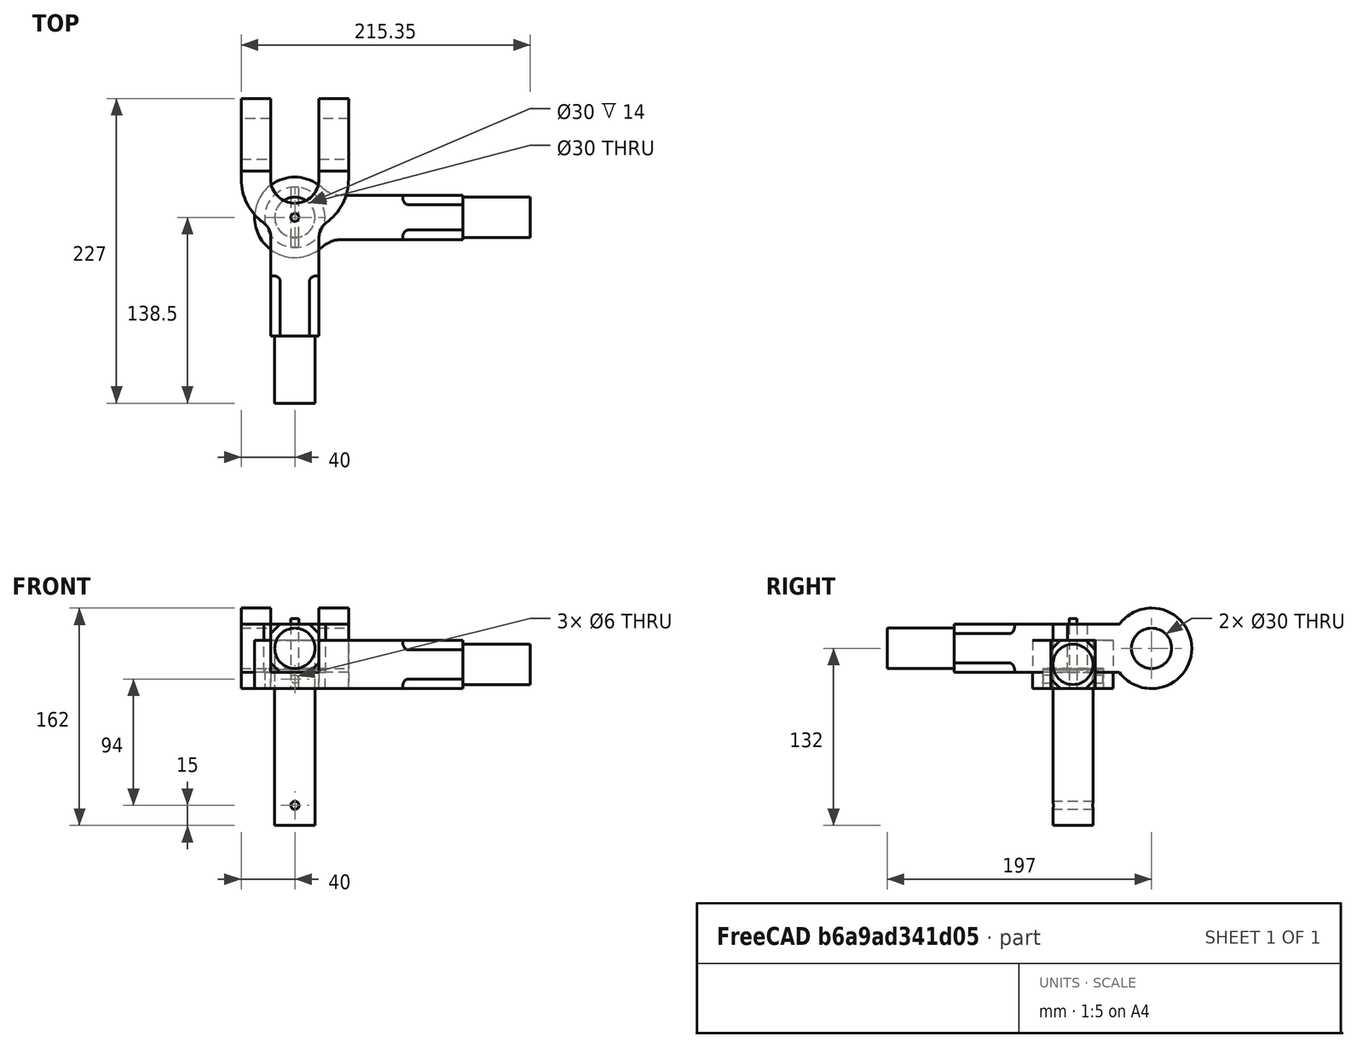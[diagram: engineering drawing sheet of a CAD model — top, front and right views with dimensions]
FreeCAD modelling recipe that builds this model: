
FCSTD DOCUMENT  (FreeCAD 1.0R39319 (Git))
Label: kunckle joint assembly and parts
License: All rights reserved
LicenseURL: https://en.wikipedia.org/wiki/All_rights_reserved
objects: TechDraw::DrawViewDimension×15, Sketcher::SketchObject×14, PartDesign::Pad×9, PartDesign::Pocket×6, PartDesign::Body×5, App::Link×5, App::FeaturePython×5, TechDraw::DrawProjGroupItem×4, PartDesign::Fillet×3, Assembly::JointGroup×1, Assembly::AssemblyObject×1, TechDraw::DrawSVGTemplate×1, TechDraw::DrawProjGroup×1, TechDraw::DrawPage×1
note: 106 computed .brp shape members not serialized (recipe doc carries the construction recipe); baked Part::Feature solids carry a one-line shape summary decoded from their .brp

FEATURE [Sketcher::SketchObject] Sketch
  ArcFitTolerance = 1e-06
  AttachmentSupport = -> [XY_Plane]
  FullyConstrained = true
  MakeInternals = false
  MapMode = 5
  sketch-geometry (7):
    g0: ArcOfCircle CenterX=0 CenterY=0 CenterZ=0 NormalX=0 NormalY=0 NormalZ=1 AngleXU=0 Radius=30 StartAngle=0.840092 EndAngle=5.44179
    g1: Circle CenterX=0 CenterY=0 CenterZ=0 NormalX=0 NormalY=0 NormalZ=1 AngleXU=0 Radius=15
    g2: LineSegment StartX=35.3005 StartY=-16.5231 StartZ=0 EndX=125.352 EndY=-16.5231 EndZ=0
    g3: LineSegment StartX=125.352 StartY=-16.5231 StartZ=0 EndX=125.352 EndY=16.4769 EndZ=0
    g4: LineSegment StartX=125.352 StartY=16.4769 StartZ=0 EndX=35.3521 EndY=16.4769 EndZ=0
    g5: ArcOfCircle CenterX=35.3521 CenterY=39.4473 CenterZ=0 NormalX=0 NormalY=0 NormalZ=1 AngleXU=0 Radius=22.9703 StartAngle=3.98168 EndAngle=4.71239
    g6: ArcOfCircle CenterX=35.3005 CenterY=-39.4934 CenterZ=0 NormalX=0 NormalY=0 NormalZ=1 AngleXU=0 Radius=22.9703 StartAngle=1.5708 EndAngle=2.30019
  constraints (18):
    c: Coincident(g0,g-1)
    c: Coincident(g1,g0)
    c: Diameter(g1) = 30
    c: Diameter(g0) = 60
    c: Coincident(g2,g3)
    c: Coincident(g3,g4)
    c: Vertical(g3)
    c: Horizontal(g2)
    c: Horizontal(g4)
    c: DistanceY(g3,g3) = 33
    c: Tangent(g0,g5) = 1.5708
    c: Tangent(g4,g5) = 1.5708
    c: Tangent(g0,g6) = 1.5708
    c: Tangent(g2,g6) = 1.5708
    c: Equal(g5,g6)
    c: Block(g5)
    c: Block(g6)
    c: DistanceX(g4,g4) = 90
FEATURE [PartDesign::Pad] Pad
  Direction = (0,0,1)
  Length = 36
  Length2 = 10
  Profile = -> Sketch
  ReferenceAxis = -> Sketch [N_Axis]
  Refine = true
  Suppressed = false
  Type = 0
FEATURE [Sketcher::SketchObject] Sketch001
  ArcFitTolerance = 1e-06
  AttachmentSupport = -> [Pad]
  ExternalGeometry = -> [Pad]
  FullyConstrained = true
  MakeInternals = false
  MapMode = 5
  Placement = pos=(125.352,0,0) rot=(0.57735,0.57735,0.57735;2.0944rad)
  sketch-geometry (1):
    g0: Circle CenterX=-0.0230899 CenterY=18 CenterZ=0 NormalX=0 NormalY=0 NormalZ=1 AngleXU=0 Radius=15
  constraints (2):
    c: Diameter(g0) = 30
    c: Symmetric(g-4,g-3,g0)
FEATURE [PartDesign::Pad] Pad001
  BaseFeature = -> Pad
  Direction = (1,0,0)
  Length = 50
  Length2 = 10
  Profile = -> Sketch001
  ReferenceAxis = -> Sketch001 [N_Axis]
  Refine = true
  Suppressed = false
  Type = 0
FEATURE [Sketcher::SketchObject] Sketch002
  ArcFitTolerance = 1e-06
  AttachmentSupport = -> [XY_Plane001]
  FullyConstrained = true
  MakeInternals = false
  MapMode = 5
  sketch-geometry (2):
    g0: Circle CenterX=0 CenterY=0 CenterZ=0 NormalX=0 NormalY=0 NormalZ=1 AngleXU=0 Radius=22.5
    g1: Circle CenterX=0 CenterY=0 CenterZ=0 NormalX=0 NormalY=0 NormalZ=1 AngleXU=0 Radius=15
  constraints (4):
    c: Coincident(g0,g-1)
    c: Coincident(g1,g0)
    c: Diameter(g0) = 45
    c: Diameter(g1) = 30
FEATURE [PartDesign::Pad] Pad002
  Direction = (0,0,1)
  Length = 14
  Length2 = 10
  Profile = -> Sketch002
  ReferenceAxis = -> Sketch002 [N_Axis]
  Refine = true
  Suppressed = false
  Type = 0
FEATURE [Sketcher::SketchObject] Sketch003
  ArcFitTolerance = 1e-06
  AttachmentSupport = -> [XZ_Plane001]
  FullyConstrained = true
  MakeInternals = false
  MapMode = 5
  Placement = pos=(0,0,0) rot=(1,0,0;1.5708rad)
  sketch-geometry (1):
    g0: Circle CenterX=0 CenterY=7 CenterZ=0 NormalX=0 NormalY=0 NormalZ=1 AngleXU=0 Radius=3
  constraints (3):
    c: PointOnObject(g0,g-2)
    c: Diameter(g0) = 6
    c: DistanceY(g-1,g0) = 7
FEATURE [PartDesign::Pocket] Pocket
  BaseFeature = -> Pad002
  Direction = (0,1,-2e-16)
  Length = 5
  Length2 = 5
  Midplane = true
  Profile = -> Sketch003
  ReferenceAxis = -> Sketch003 [N_Axis]
  Refine = true
  Suppressed = false
  Type = 1
FEATURE [PartDesign::Body] Body001  label="Collar"
  AllowCompound = false
  Group = -> [Sketch002,Pad002,Sketch003,Pocket]
  Origin = -> Origin001
  Tip = -> Pocket
FEATURE [Sketcher::SketchObject] Sketch004
  ArcFitTolerance = 1e-06
  AttachmentSupport = -> [XY_Plane002]
  FullyConstrained = true
  MakeInternals = false
  MapMode = 5
  sketch-geometry (1):
    g0: Circle CenterX=0 CenterY=0 CenterZ=0 NormalX=0 NormalY=0 NormalZ=1 AngleXU=0 Radius=22.5
  constraints (2):
    c: Coincident(g0,g-1)
    c: Diameter(g0) = 45
FEATURE [PartDesign::Pad] Pad003
  Direction = (0,0,1)
  Length = 15
  Length2 = 10
  Profile = -> Sketch004
  ReferenceAxis = -> Sketch004 [N_Axis]
  Refine = true
  Suppressed = false
  Type = 0
FEATURE [Sketcher::SketchObject] Sketch005
  ArcFitTolerance = 1e-06
  AttachmentSupport = -> [Pad003]
  FullyConstrained = true
  MakeInternals = false
  MapMode = 5
  Placement = pos=(0,0,0) rot=(1,0,0;3.14159rad)
  sketch-geometry (1):
    g0: Circle CenterX=0 CenterY=0 CenterZ=0 NormalX=0 NormalY=0 NormalZ=1 AngleXU=0 Radius=15
  constraints (2):
    c: Coincident(g0,g-1)
    c: Diameter(g0) = 30
FEATURE [PartDesign::Pad] Pad004
  BaseFeature = -> Pad003
  Direction = (0,0,-1)
  Length = 102
  Length2 = 10
  Profile = -> Sketch005
  ReferenceAxis = -> Sketch005 [N_Axis]
  Refine = true
  Suppressed = false
  Type = 0
FEATURE [Sketcher::SketchObject] Sketch006
  ArcFitTolerance = 1e-06
  AttachmentSupport = -> [XZ_Plane002]
  ExternalGeometry = -> [Pad004]
  FullyConstrained = true
  MakeInternals = false
  MapMode = 5
  Placement = pos=(0,0,0) rot=(1,0,0;1.5708rad)
  sketch-geometry (1):
    g0: Circle CenterX=0 CenterY=-87 CenterZ=0 NormalX=0 NormalY=0 NormalZ=1 AngleXU=0 Radius=3
  constraints (3):
    c: PointOnObject(g0,g-2)
    c: Diameter(g0) = 6
    c: Distance(g0,g-3) = 15
FEATURE [PartDesign::Pocket] Pocket001
  BaseFeature = -> Pad004
  Direction = (0,1,-2e-16)
  Length = 5
  Length2 = 5
  Midplane = true
  Profile = -> Sketch006
  ReferenceAxis = -> Sketch006 [N_Axis]
  Refine = true
  Suppressed = false
  Type = 1
FEATURE [PartDesign::Body] Body002  label="kunckle_pin"
  AllowCompound = false
  Group = -> [Sketch004,Pad003,Sketch005,Pad004,Sketch006,Pocket001]
  Origin = -> Origin002
  Tip = -> Pocket001
FEATURE [Sketcher::SketchObject] Sketch007
  ArcFitTolerance = 1e-06
  AttachmentSupport = -> [XY_Plane003]
  FullyConstrained = true
  MakeInternals = false
  MapMode = 5
  sketch-geometry (1):
    g0: Circle CenterX=0 CenterY=0 CenterZ=0 NormalX=0 NormalY=0 NormalZ=1 AngleXU=0 Radius=3
  constraints (2):
    c: Coincident(g0,g-1)
    c: Diameter(g0) = 6
FEATURE [PartDesign::Pad] Pad005
  Direction = (0,0,1)
  Length = 52
  Length2 = 10
  Profile = -> Sketch007
  ReferenceAxis = -> Sketch007 [N_Axis]
  Refine = true
  Suppressed = false
  Type = 0
FEATURE [PartDesign::Body] Body003  label="taper_pin"
  AllowCompound = false
  Group = -> [Sketch007,Pad005]
  Origin = -> Origin003
  Tip = -> Pad005
FEATURE [Sketcher::SketchObject] Sketch008
  ArcFitTolerance = 1e-06
  AttachmentSupport = -> [Pad001]
  ExternalGeometry = -> [Pad001]
  FullyConstrained = true
  MakeInternals = false
  MapMode = 5
  Placement = pos=(125.352,0,0) rot=(0.57735,0.57735,0.57735;2.0944rad)
  sketch-geometry (12):
    g0: LineSegment StartX=-16.5231 StartY=36 StartZ=0 EndX=-16.5231 EndY=28.9289 EndZ=0
    g1: LineSegment StartX=-16.5231 StartY=28.9289 StartZ=0 EndX=-9.45202 EndY=36 EndZ=0
    g2: LineSegment StartX=-16.5231 StartY=36 StartZ=0 EndX=-9.45202 EndY=36 EndZ=0
    g3: LineSegment StartX=-16.5231 StartY=7.07107 StartZ=0 EndX=-16.5231 EndY=0 EndZ=0
    g4: LineSegment StartX=-16.5231 StartY=0 StartZ=0 EndX=-9.45202 EndY=0 EndZ=0
    g5: LineSegment StartX=-9.45202 StartY=0 StartZ=0 EndX=-16.5231 EndY=7.07107 EndZ=0
    g6: LineSegment StartX=16.5231 StartY=28.9753 StartZ=0 EndX=9.45202 EndY=36 EndZ=0
    g7: LineSegment StartX=16.4769 StartY=36 StartZ=0 EndX=9.45202 EndY=36 EndZ=0
    g8: LineSegment StartX=16.4769 StartY=36 StartZ=0 EndX=16.5231 EndY=28.9753 EndZ=0
    g9: LineSegment StartX=9.40584 StartY=0 StartZ=0 EndX=16.4769 EndY=7.07107 EndZ=0
    g10: LineSegment StartX=16.4769 StartY=7.07107 StartZ=0 EndX=16.4769 EndY=0 EndZ=0
    g11: LineSegment StartX=16.4769 StartY=0 StartZ=0 EndX=9.40584 EndY=0 EndZ=0
  constraints (30):
    c: Coincident(g0,g-5)
    c: PointOnObject(g0,g-5)
    c: Coincident(g1,g0)
    c: Coincident(g2,g0)
    c: Coincident(g2,g1)
    c: PointOnObject(g1,g-3)
    c: PointOnObject(g3,g-5)
    c: Coincident(g3,g-5)
    c: Coincident(g3,g4)
    c: PointOnObject(g4,g-1)
    c: Coincident(g4,g5)
    c: Coincident(g5,g3)
    c: Equal(g2,g0)
    c: Distance(g1,g1) = 10
    c: Distance(g5,g5) = 10
    c: Equal(g3,g4)
    c: Coincident(g6,g8)
    c: Coincident(g7,g8)
    c: Coincident(g7,g6)
    c: Equal(g7,g8)
    c: Coincident(g10,g11)
    c: Coincident(g11,g9)
    c: Coincident(g9,g10)
    c: Equal(g10,g11)
    c: Block(g6)
    c: Coincident(g10,g-4)
    c: PointOnObject(g9,g-1)
    c: Coincident(g7,g-4)
    c: PointOnObject(g9,g-4)
    c: Distance(g9,g9) = 10
FEATURE [PartDesign::Pocket] Pocket002
  BaseFeature = -> Pad001
  Direction = (-1,0,0)
  Length = 45
  Length2 = 5
  Profile = -> Sketch008
  ReferenceAxis = -> Sketch008 [N_Axis]
  Refine = true
  Suppressed = false
  Type = 0
FEATURE [PartDesign::Fillet] Fillet
  Base = -> Pocket002 [Edge46,Edge44]
  BaseFeature = -> Pocket002
  Radius = 4
  Refine = true
  SupportTransform = false
  Suppressed = false
  UseAllEdges = false
FEATURE [PartDesign::Fillet] Fillet001
  Base = -> Fillet [Edge36,Edge52]
  BaseFeature = -> Fillet
  Radius = 4
  Refine = true
  SupportTransform = false
  Suppressed = false
  UseAllEdges = false
FEATURE [PartDesign::Body] Body  label="Single_eye"
  AllowCompound = false
  Group = -> [Sketch,Pad,Sketch001,Pad001,Sketch008,Pocket002,Fillet,Fillet001]
  Origin = -> Origin
  Tip = -> Fillet001
FEATURE [Sketcher::SketchObject] Sketch009
  ArcFitTolerance = 1e-06
  AttachmentSupport = -> [XY_Plane004]
  FullyConstrained = true
  MakeInternals = false
  MapMode = 5
  sketch-geometry (5):
    g0: LineSegment StartX=-40 StartY=88.5 StartZ=0 EndX=-40 EndY=-88.5 EndZ=0
    g1: LineSegment StartX=-40 StartY=-88.5 StartZ=0 EndX=40 EndY=-88.5 EndZ=0
    g2: LineSegment StartX=40 StartY=-88.5 StartZ=0 EndX=40 EndY=88.5 EndZ=0
    g3: LineSegment StartX=40 StartY=88.5 StartZ=0 EndX=-40 EndY=88.5 EndZ=0
    g4: GeomPoint [constr] X=0 Y=0 Z=0
  constraints (12):
    c: Coincident(g0,g1)
    c: Coincident(g1,g2)
    c: Coincident(g2,g3)
    c: Coincident(g3,g0)
    c: Vertical(g0)
    c: Vertical(g2)
    c: Horizontal(g1)
    c: Horizontal(g3)
    c: Symmetric(g2,g0,g4)
    c: Coincident(g4,g-1)
    c: DistanceY(g2,g2) = 177
    c: DistanceX(g3,g3) = 80
FEATURE [PartDesign::Pad] Pad006
  Direction = (0,0,1)
  Length = 60
  Length2 = 10
  Profile = -> Sketch009
  ReferenceAxis = -> Sketch009 [N_Axis]
  Refine = true
  Suppressed = false
  Type = 0
FEATURE [PartDesign::Pad] Pad007
  BaseFeature = -> Pad006
  Direction = (0,0,1)
  Length = 5
  Length2 = 10
  Profile = -> Sketch009
  ReferenceAxis = -> Sketch009 [N_Axis]
  Refine = true
  Suppressed = false
  Type = 0
FEATURE [Sketcher::SketchObject] Sketch010
  ArcFitTolerance = 1e-06
  AttachmentSupport = -> [Pad006]
  ExternalGeometry = -> [Pad006]
  FullyConstrained = false
  MakeInternals = false
  MapMode = 5
  Placement = pos=(0,0,0) rot=(1,0,0;3.14159rad)
  sketch-geometry (14):
    g0: ArcOfCircle CenterX=0 CenterY=-28.5 CenterZ=0 NormalX=0 NormalY=0 NormalZ=1 AngleXU=0 Radius=40 StartAngle=-9e-16 EndAngle=0.954279
    g1: ArcOfCircle CenterX=0 CenterY=-28.5 CenterZ=0 NormalX=0 NormalY=0 NormalZ=1 AngleXU=0 Radius=18 StartAngle=2e-16 EndAngle=3.14159
    g2: LineSegment StartX=-18 StartY=88.5 StartZ=0 EndX=-18 EndY=15.1917 EndZ=0
    g3: LineSegment StartX=18 StartY=88.5 StartZ=0 EndX=18 EndY=14.9616 EndZ=0
    g4: LineSegment StartX=-18 StartY=-28.5 StartZ=0 EndX=-18 EndY=-88.5 EndZ=0
    g5: LineSegment StartX=18 StartY=-28.5 StartZ=0 EndX=18 EndY=-88.5 EndZ=0
    g6: LineSegment StartX=-18 StartY=-88.5 StartZ=0 EndX=18 EndY=-88.5 EndZ=0
    g7: LineSegment StartX=-18 StartY=88.5 StartZ=0 EndX=-40 EndY=88.5 EndZ=0
    g8: LineSegment StartX=-40 StartY=88.5 StartZ=0 EndX=-40 EndY=-28.5 EndZ=0
    g9: LineSegment StartX=18 StartY=88.5 StartZ=0 EndX=40 EndY=88.5 EndZ=0
    g10: LineSegment StartX=40 StartY=88.5 StartZ=0 EndX=40 EndY=-28.5 EndZ=0
    g11: ArcOfCircle CenterX=0 CenterY=-28.5 CenterZ=0 NormalX=0 NormalY=0 NormalZ=1 AngleXU=0 Radius=40 StartAngle=2.19011 EndAngle=3.14159
    g12: ArcOfCircle CenterX=31.2806 CenterY=14.625 CenterZ=0 NormalX=0 NormalY=0 NormalZ=1 AngleXU=0 Radius=13.2849 StartAngle=3.11625 EndAngle=4.05167
    g13: ArcOfCircle CenterX=-31.2733 CenterY=14.636 CenterZ=0 NormalX=0 NormalY=0 NormalZ=1 AngleXU=0 Radius=13.2849 StartAngle=5.36376 EndAngle=6.32502
  constraints (33):
    c: Coincident(g1,g0)
    c: Diameter(g1) = 36
    c: PointOnObject(g2,g-5)
    c: Vertical(g2)
    c: PointOnObject(g3,g-5)
    c: Vertical(g3)
    c: PointOnObject(g4,g-6)
    c: Vertical(g4)
    c: PointOnObject(g5,g-6)
    c: Vertical(g5)
    c: Distance(g3,g2) = 36
    c: Distance(g-2,g2) = 18
    c: Tangent(g1,g4) = -1.5708
    c: Tangent(g1,g5) = 1.5708
    c: Coincident(g6,g4)
    c: Coincident(g6,g5)
    c: Coincident(g2,g7)
    c: Coincident(g7,g-5)
    c: Coincident(g7,g8)
    c: Coincident(g3,g9)
    c: Coincident(g9,g-5)
    c: Coincident(g9,g10)
    c: Vertical(g10)
    c: Block(g7)
    c: Block(g8)
    c: Block(g10)
    c: Block(g11)
    c: Block(g0)
    c: Equal(g13,g12)
    c: Coincident(g3,g12)
    c: Coincident(g12,g0)
    c: Coincident(g13,g2)
    c: Coincident(g11,g13)
FEATURE [PartDesign::Pocket] Pocket003
  BaseFeature = -> Pad007
  Direction = (0,0,1)
  Length = 5
  Length2 = 5
  Profile = -> Sketch010
  ReferenceAxis = -> Sketch010 [N_Axis]
  Refine = true
  Suppressed = false
  Type = 1
FEATURE [Sketcher::SketchObject] Sketch011
  ArcFitTolerance = 1e-06
  AttachmentSupport = -> [Pocket003]
  ExternalGeometry = -> [Pocket003]
  FullyConstrained = false
  MakeInternals = false
  MapMode = 5
  Placement = pos=(40,0,0) rot=(0.57735,0.57735,0.57735;2.0944rad)
  sketch-geometry (11):
    g0: ArcOfCircle CenterX=58.5 CenterY=30 CenterZ=0 NormalX=0 NormalY=0 NormalZ=1 AngleXU=0 Radius=30 StartAngle=3.78509 EndAngle=8.78128
    g1: Circle CenterX=58.5 CenterY=30 CenterZ=0 NormalX=0 NormalY=0 NormalZ=1 AngleXU=0 Radius=15
    g2: LineSegment StartX=34.5 StartY=48 StartZ=0 EndX=-88.5 EndY=48 EndZ=0
    g3: LineSegment StartX=-88.5 StartY=12 StartZ=0 EndX=34.5 EndY=12 EndZ=0
    g4: LineSegment StartX=-88.5 StartY=12 StartZ=0 EndX=-88.5 EndY=0 EndZ=0
    g5: LineSegment StartX=-88.5 StartY=0 StartZ=0 EndX=58.5 EndY=0 EndZ=0
    g6: LineSegment StartX=-88.5 StartY=48 StartZ=0 EndX=-88.5 EndY=60 EndZ=0
    g7: LineSegment StartX=-88.5 StartY=60 StartZ=0 EndX=58.5 EndY=60 EndZ=0
    g8: LineSegment StartX=58.5 StartY=60 StartZ=0 EndX=88.5 EndY=60 EndZ=0
    g9: LineSegment StartX=88.5 StartY=60 StartZ=0 EndX=88.5 EndY=0 EndZ=0
    g10: LineSegment StartX=88.5 StartY=0 StartZ=0 EndX=58.5 EndY=0 EndZ=0
  constraints (25):
    c: Coincident(g1,g0)
    c: Diameter(g0) = 60
    c: Diameter(g1) = 30
    c: Tangent(g0,g-4)
    c: Tangent(g-3,g0)
    c: Horizontal(g2)
    c: Horizontal(g3)
    c: Distance(g3,g2) = 36
    c: PointOnObject(g2,g-5)
    c: Coincident(g0,g2)
    c: Coincident(g0,g3)
    c: Coincident(g4,g-5)
    c: Coincident(g4,g5)
    c: PointOnObject(g5,g0)
    c: Horizontal(g5)
    c: Coincident(g6,g2)
    c: Coincident(g6,g-5)
    c: Coincident(g7,g6)
    c: Symmetric(g-3,g-3,g7)
    c: Coincident(g8,g-4)
    c: Horizontal(g8)
    c: Coincident(g8,g9)
    c: Coincident(g9,g-4)
    c: Coincident(g9,g10)
    c: Coincident(g10,g5)
FEATURE [PartDesign::Pocket] Pocket004
  BaseFeature = -> Pocket003
  Direction = (-1,0,0)
  Length = 5
  Length2 = 5
  Profile = -> Sketch011
  ReferenceAxis = -> Sketch011 [N_Axis]
  Refine = true
  Suppressed = false
  Type = 1
FEATURE [Sketcher::SketchObject] Sketch012
  ArcFitTolerance = 1e-06
  AttachmentSupport = -> [Pocket004]
  ExternalGeometry = -> [Pocket004]
  FullyConstrained = true
  MakeInternals = false
  MapMode = 5
  Placement = pos=(0,-88.5,0) rot=(1,0,0;1.5708rad)
  sketch-geometry (1):
    g0: Circle CenterX=2.4e-15 CenterY=30 CenterZ=0 NormalX=0 NormalY=0 NormalZ=1 AngleXU=0 Radius=15
  constraints (2):
    c: Symmetric(g-3,g-4,g0)
    c: Diameter(g0) = 30
FEATURE [PartDesign::Pad] Pad008
  BaseFeature = -> Pocket004
  Direction = (0,-1,2e-16)
  Length = 50
  Length2 = 10
  Profile = -> Sketch012
  ReferenceAxis = -> Sketch012 [N_Axis]
  Refine = true
  Suppressed = false
  Type = 0
FEATURE [Sketcher::SketchObject] Sketch013
  ArcFitTolerance = 1e-06
  AttachmentSupport = -> [Pad008]
  ExternalGeometry = -> [Pad008]
  FullyConstrained = true
  MakeInternals = false
  MapMode = 5
  Placement = pos=(0,-88.5,0) rot=(1,0,0;1.5708rad)
  sketch-geometry (12):
    g0: LineSegment StartX=-18 StartY=48 StartZ=0 EndX=-18 EndY=40.9289 EndZ=0
    g1: LineSegment StartX=-18 StartY=40.9289 StartZ=0 EndX=-10.9289 EndY=48 EndZ=0
    g2: LineSegment StartX=-10.9289 StartY=48 StartZ=0 EndX=-18 EndY=48 EndZ=0
    g3: LineSegment StartX=10.9289 StartY=48 StartZ=0 EndX=18 EndY=40.9289 EndZ=0
    g4: LineSegment StartX=18 StartY=40.9289 StartZ=0 EndX=18 EndY=48 EndZ=0
    g5: LineSegment StartX=18 StartY=48 StartZ=0 EndX=10.9289 EndY=48 EndZ=0
    g6: LineSegment StartX=-18 StartY=19.0711 StartZ=0 EndX=-18 EndY=12 EndZ=0
    g7: LineSegment StartX=-18 StartY=12 StartZ=0 EndX=-10.9289 EndY=12 EndZ=0
    g8: LineSegment StartX=-10.9289 StartY=12 StartZ=0 EndX=-18 EndY=19.0711 EndZ=0
    g9: LineSegment StartX=18 StartY=19.0711 StartZ=0 EndX=18 EndY=12 EndZ=0
    g10: LineSegment StartX=18 StartY=12 StartZ=0 EndX=10.9289 EndY=12 EndZ=0
    g11: LineSegment StartX=10.9289 StartY=12 StartZ=0 EndX=18 EndY=19.0711 EndZ=0
  constraints (32):
    c: Coincident(g-3,g0)
    c: Vertical(g0)
    c: Coincident(g0,g1)
    c: PointOnObject(g1,g-3)
    c: Coincident(g1,g2)
    c: Coincident(g2,g0)
    c: PointOnObject(g3,g-3)
    c: PointOnObject(g3,g-4)
    c: Coincident(g3,g4)
    c: Coincident(g4,g-4)
    c: Coincident(g4,g5)
    c: Coincident(g5,g3)
    c: PointOnObject(g6,g-6)
    c: Coincident(g6,g-6)
    c: Coincident(g6,g7)
    c: PointOnObject(g7,g-5)
    c: Coincident(g7,g8)
    c: Coincident(g8,g6)
    c: PointOnObject(g9,g-4)
    c: Coincident(g9,g-5)
    c: Coincident(g9,g10)
    c: PointOnObject(g10,g-5)
    c: Coincident(g10,g11)
    c: Coincident(g11,g9)
    c: Distance(g1,g1) = 10
    c: Equal(g0,g2)
    c: Equal(g6,g7)
    c: Equal(g10,g9)
    c: Distance(g3,g3) = 10
    c: Distance(g11,g11) = 10
    c: Distance(g8,g8) = 10
    c: Equal(g4,g5)
FEATURE [PartDesign::Pocket] Pocket005
  BaseFeature = -> Pad008
  Direction = (0,1,-2e-16)
  Length = 45
  Length2 = 5
  Profile = -> Sketch013
  ReferenceAxis = -> Sketch013 [N_Axis]
  Refine = true
  Suppressed = false
  Type = 0
FEATURE [PartDesign::Fillet] Fillet002
  Base = -> Pocket005 [Edge83,Edge84,Edge64,Edge72]
  BaseFeature = -> Pocket005
  Radius = 4
  Refine = true
  SupportTransform = false
  Suppressed = false
  UseAllEdges = false
FEATURE [PartDesign::Body] Body004  label="double eye"
  AllowCompound = false
  Group = -> [Sketch009,Pad006,Pad007,Sketch010,Pocket003,Sketch011,Pocket004,Sketch012,Pad008,Sketch013,Pocket005,Fillet002]
  Origin = -> Origin004
  Tip = -> Fillet002
FEATURE [App::Link] kunckle_pin  label="kunckle_pin001"
  LinkedObject = -> Body002
FEATURE [App::FeaturePython] GroundedJoint  # Assembly grounded joint (typed FeaturePython)
  ObjectToGround = -> kunckle_pin
FEATURE [App::Link] double_eye  label="double eye001"
  LinkPlacement = pos=(-30.1645,58.4153,-40) rot=(0.707106,0.000995,0.707106;3.14358rad)
  LinkedObject = -> Body004
  Placement = pos=(-30.1645,58.4153,-40) rot=(0.707106,0.000995,0.707106;3.14358rad)
FEATURE [App::Link] Single_eye  label="Single_eye001"
  LinkPlacement = pos=(0,0,-57.7859) rot=(0,0,-1;1.5708rad)
  LinkedObject = -> Body
  Placement = pos=(0,0,-57.7859) rot=(0,0,-1;1.5708rad)
FEATURE [App::Link] Collar  label="Collar001"
  LinkPlacement = pos=(0,0,-94) rot=(0,0,1;0rad)
  LinkedObject = -> Body001
  Placement = pos=(0,0,-94) rot=(0,0,1;0rad)
FEATURE [App::Link] taper_pin  label="taper_pin001"
  LinkPlacement = pos=(-2e-16,-25.3761,-87) rot=(0.998783,0.034878,0.034878;4.71117rad)
  LinkedObject = -> Body003
  Placement = pos=(-2e-16,-25.3761,-87) rot=(0.998783,0.034878,0.034878;4.71117rad)
FEATURE [App::FeaturePython] Joint  label="Revolute"  # Assembly joint (typed FeaturePython)
  Activated = true
  AngleMax = 40
  AngleMin = -140
  Detach1 = false
  Detach2 = false
  Distance = 0
  Distance2 = 0
  EnableAngleMax = true
  EnableAngleMin = true
  EnableLengthMax = false
  EnableLengthMin = false
  JointType = 1 (Revolute)
  LengthMax = 0
  LengthMin = 0
  Placement2 = pos=(40,58.5,30) rot=(-0.57735,-0.57735,-0.57735;4.18879rad)
  Reference1 = -> Assembly [kunckle_pin.Pocket001.Edge2,kunckle_pin.Pocket001.Edge2]
  Reference2 = -> Assembly [double_eye.Fillet002.Edge50,double_eye.Fillet002.Edge50]
FEATURE [App::FeaturePython] Joint001  label="Revolute001"  # Assembly joint (typed FeaturePython)
  Activated = true
  AngleMax = 90
  AngleMin = -10
  Detach1 = false
  Detach2 = false
  Distance = 0
  Distance2 = 0
  EnableAngleMax = true
  EnableAngleMin = true
  EnableLengthMax = false
  EnableLengthMin = false
  JointType = 1 (Revolute)
  LengthMax = 0
  LengthMin = 0
  Offset2 = pos=(0,0,-29) rot=(0,0,1;0rad)
  Placement1 = pos=(0,0,36) rot=(0,0,1;0rad)
  Placement2 = pos=(0,0,-21.7859) rot=(1,0,0;3.14159rad)
  Reference1 = -> Assembly [Single_eye.Fillet001.Edge48,Single_eye.Fillet001.Edge48]
  Reference2 = -> Assembly [kunckle_pin.Pocket001.Face4,kunckle_pin.Pocket001.Face4]
FEATURE [App::FeaturePython] Joint002  label="Fixed"  # Assembly joint (typed FeaturePython)
  Activated = true
  AngleMax = 0
  AngleMin = 0
  Detach1 = false
  Detach2 = false
  Distance = 0
  Distance2 = 0
  EnableAngleMax = false
  EnableAngleMin = false
  EnableLengthMax = false
  EnableLengthMin = false
  JointType = 0 (Fixed)
  LengthMax = 0
  LengthMin = 0
  Offset2 = pos=(0,0,-8) rot=(0,0,1;0rad)
  Placement1 = pos=(0,0,-102) rot=(1,0,0;3.14159rad)
  Placement2 = pos=(0,0,-8) rot=(0,0,1;0rad)
  Reference1 = -> Assembly [kunckle_pin.Pocket001.Edge6,kunckle_pin.Pocket001.Edge6]
  Reference2 = -> Assembly [Collar.Pocket.Edge1,Collar.Pocket.Edge1]
FEATURE [App::FeaturePython] Joint003  label="Fixed001"  # Assembly joint (typed FeaturePython)
  Activated = true
  AngleMax = 0
  AngleMin = 0
  Detach1 = false
  Detach2 = false
  Distance = 0
  Distance2 = 0
  EnableAngleMax = false
  EnableAngleMin = false
  EnableLengthMax = false
  EnableLengthMin = false
  JointType = 0 (Fixed)
  LengthMax = 0
  LengthMin = 0
  Offset2 = pos=(0,0,18) rot=(0,0,1;0.069813rad)
  Placement1 = pos=(0,18.6239,7) rot=(1,0,0;1.5708rad)
  Placement2 = pos=(0,0,44) rot=(0,0,-1;6.21337rad)
  Reference1 = -> Assembly [Collar.Pocket.Face4,Collar.Pocket.Face4]
  Reference2 = -> Assembly [taper_pin.Pad005.Face1,taper_pin.Pad005.Face1]
FEATURE [Assembly::JointGroup] Joints
  Group = -> [GroundedJoint,Joint,Joint001,Joint002,Joint003]
FEATURE [Assembly::AssemblyObject] Assembly
  Group = -> [Joints,kunckle_pin,GroundedJoint,double_eye,Single_eye,Collar,taper_pin,Joint,Joint001,Joint002,Joint003]
  Origin = -> Origin005
  Type = Assembly
FEATURE [TechDraw::DrawSVGTemplate] Template
  Height = 210
  Orientation = 1
  Template = D:/New folder/FreeCAD 1.0/data/Mod/TechDraw/Templates/A4_Landscape_TD.svg
  Width = 297
FEATURE [TechDraw::DrawProjGroupItem] View  label="Front"
  CoarseView = false
  Direction = (0,-1,0)
  Focus = 100
  HardHidden = false
  IsoCount = 0
  IsoHidden = false
  IsoVisible = false
  LockPosition = true
  Perspective = false
  Rotation = 0
  RotationVector = (1,0,0)
  Scale = 0.2
  ScaleType = 2
  ScrubCount = 1
  SeamHidden = false
  SeamVisible = false
  SmoothHidden = false
  SmoothVisible = true
  Source = -> [Assembly]
  Type = 0
  X = 0
  XDirection = (1,0,0)
  Y = 0
FEATURE [TechDraw::DrawProjGroupItem] ProjItem  label="Top"
  CoarseView = false
  Direction = (0,0,1)
  Focus = 100
  HardHidden = false
  IsoCount = 0
  IsoHidden = false
  IsoVisible = false
  LockPosition = false
  Perspective = false
  Rotation = 0
  RotationVector = (1,0,0)
  Scale = 0.2
  ScaleType = 0
  ScrubCount = 1
  SeamHidden = false
  SeamVisible = false
  SmoothHidden = false
  SmoothVisible = true
  Source = -> [Assembly]
  Type = 4
  X = 0
  XDirection = (1,0,0)
  Y = -82.3212
FEATURE [TechDraw::DrawProjGroupItem] ProjItem001  label="Left"
  CoarseView = false
  Direction = (-1,-1e-16,0)
  Focus = 100
  HardHidden = false
  IsoCount = 0
  IsoHidden = false
  IsoVisible = false
  LockPosition = false
  Perspective = false
  Rotation = 0
  RotationVector = (1,0,0)
  Scale = 0.2
  ScaleType = 0
  ScrubCount = 1
  SeamHidden = false
  SeamVisible = false
  SmoothHidden = false
  SmoothVisible = true
  Source = -> [Assembly]
  Type = 1
  X = 95.769
  XDirection = (1e-16,-1,0)
  Y = 0
FEATURE [TechDraw::DrawProjGroupItem] ProjItem002  label="FrontTopLeft"
  CoarseView = false
  Direction = (-0.57735,-0.57735,0.57735)
  Focus = 100
  HardHidden = false
  IsoCount = 0
  IsoHidden = false
  IsoVisible = false
  LockPosition = false
  Perspective = false
  Rotation = 0
  RotationVector = (1,0,0)
  Scale = 0.2
  ScaleType = 0
  ScrubCount = 1
  SeamHidden = false
  SeamVisible = false
  SmoothHidden = false
  SmoothVisible = true
  Source = -> [Assembly]
  Type = 6
  X = 93.4713
  XDirection = (0.707107,-0.707107,0)
  Y = -63.1734
FEATURE [TechDraw::DrawProjGroup] ProjGroup
  Anchor = -> View
  AutoDistribute = true
  LockPosition = false
  ProjectionType = 0
  Rotation = 0
  Scale = 0.2
  ScaleType = 2
  Source = -> [Assembly]
  Views = -> [View,ProjItem,ProjItem001,ProjItem002]
  X = 52.7228
  Y = 165.705
  spacingX = 15
  spacingY = 15
FEATURE [TechDraw::DrawViewDimension] Dimension
  AngleOverride = false
  Arbitrary = false
  ArbitraryTolerances = false
  BoxCorners = (2) [(-7.5,-14.625,-1e-07),(7.5,14.625,1e-07)]
  EqualTolerance = true
  ExtensionAngle = 0
  FormatSpec = %.2w
  FormatSpecOverTolerance = %+.2w
  FormatSpecUnderTolerance = %+.2w
  Inverted = false
  LineAngle = 0
  LockPosition = false
  MeasureType = 1
  OverTolerance = 0
  References2D = -> [View]
  Rotation = 0
  ScaleType = 0
  TheoreticalExact = false
  Type = 1
  UnderTolerance = 0
  X = 6.44392
  Y = 29.7996
FEATURE [TechDraw::DrawViewDimension] Dimension001
  AngleOverride = false
  Arbitrary = false
  ArbitraryTolerances = false
  BoxCorners = (2) [(-7.5,-14.625,-1e-07),(7.5,14.625,1e-07)]
  EqualTolerance = true
  ExtensionAngle = 0
  FormatSpec = ⌀%.2w
  FormatSpecOverTolerance = %+.2w
  FormatSpecUnderTolerance = %+.2w
  Inverted = false
  LineAngle = 0
  LockPosition = false
  MeasureType = 1
  OverTolerance = 0
  References2D = -> [View]
  Rotation = 0
  ScaleType = 0
  TheoreticalExact = false
  Type = 5
  UnderTolerance = 0
  X = 20.9376
  Y = 18.3597
FEATURE [TechDraw::DrawViewDimension] Dimension002
  AngleOverride = false
  Arbitrary = false
  ArbitraryTolerances = false
  BoxCorners = (2) [(-7.5,-14.625,-1e-07),(7.5,14.625,1e-07)]
  EqualTolerance = true
  ExtensionAngle = 0
  FormatSpec = %.2w
  FormatSpecOverTolerance = %+.2w
  FormatSpecUnderTolerance = %+.2w
  Inverted = false
  LineAngle = 0
  LockPosition = false
  MeasureType = 1
  OverTolerance = 0
  References2D = -> [View]
  Rotation = 0
  ScaleType = 0
  TheoreticalExact = false
  Type = 0
  UnderTolerance = 0
  X = 16.1663
  Y = -7.75115
FEATURE [TechDraw::DrawViewDimension] Dimension003
  AngleOverride = false
  Arbitrary = false
  ArbitraryTolerances = false
  BoxCorners = (2) [(-7.5,-14.625,-1e-07),(7.5,14.625,1e-07)]
  EqualTolerance = true
  ExtensionAngle = 0
  FormatSpec = %.2w
  FormatSpecOverTolerance = %+.2w
  FormatSpecUnderTolerance = %+.2w
  Inverted = false
  LineAngle = 0
  LockPosition = false
  MeasureType = 1
  OverTolerance = 0
  References2D = -> [View]
  Rotation = 0
  ScaleType = 0
  TheoreticalExact = false
  Type = 0
  UnderTolerance = 0
  X = -22.6491
  Y = 0.875
FEATURE [TechDraw::DrawViewDimension] Dimension004
  AngleOverride = false
  Arbitrary = false
  ArbitraryTolerances = false
  BoxCorners = (2) [(-7.5,-14.625,-1e-07),(7.5,14.625,1e-07)]
  EqualTolerance = true
  ExtensionAngle = 0
  FormatSpec = %.2w
  FormatSpecOverTolerance = %+.2w
  FormatSpecUnderTolerance = %+.2w
  Inverted = false
  LineAngle = 0
  LockPosition = false
  MeasureType = 1
  OverTolerance = 0
  References2D = -> [View]
  Rotation = 0
  ScaleType = 0
  TheoreticalExact = false
  Type = 0
  UnderTolerance = 0
  X = -22.6491
  Y = -18.8272
FEATURE [TechDraw::DrawViewDimension] Dimension005
  AngleOverride = false
  Arbitrary = false
  ArbitraryTolerances = false
  BoxCorners = (2) [(-7.5,-14.625,-1e-07),(7.5,14.625,1e-07)]
  EqualTolerance = true
  ExtensionAngle = 0
  FormatSpec = R%.2w
  FormatSpecOverTolerance = %+.2w
  FormatSpecUnderTolerance = %+.2w
  Inverted = false
  LineAngle = 0
  LockPosition = false
  MeasureType = 1
  OverTolerance = 0
  References2D = -> [View]
  Rotation = 0
  ScaleType = 0
  TheoreticalExact = false
  Type = 4
  UnderTolerance = 0
  X = 19.2482
  Y = 5.12796
FEATURE [TechDraw::DrawViewDimension] Dimension006
  AngleOverride = false
  Arbitrary = false
  ArbitraryTolerances = false
  BoxCorners = (2) [(-6,-37.2394,-1e-07),(6,37.2394,1e-07)]
  EqualTolerance = true
  ExtensionAngle = 0
  FormatSpec = %.2w
  FormatSpecOverTolerance = %+.2w
  FormatSpecUnderTolerance = %+.2w
  Inverted = false
  LineAngle = 0
  LockPosition = false
  MeasureType = 1
  OverTolerance = 0
  References2D = -> [ProjItem]
  Rotation = 0
  ScaleType = 0
  TheoreticalExact = false
  Type = 2
  UnderTolerance = 0
  X = 14.0174
  Y = 40.2992
FEATURE [TechDraw::DrawViewDimension] Dimension007
  AngleOverride = false
  Arbitrary = false
  ArbitraryTolerances = false
  BoxCorners = (2) [(-6,-37.2394,-1e-07),(6,37.2394,1e-07)]
  EqualTolerance = true
  ExtensionAngle = 0
  FormatSpec = %.2w
  FormatSpecOverTolerance = %+.2w
  FormatSpecUnderTolerance = %+.2w
  Inverted = false
  LineAngle = 0
  LockPosition = false
  MeasureType = 1
  OverTolerance = 0
  References2D = -> [ProjItem]
  Rotation = 0
  ScaleType = 0
  TheoreticalExact = false
  Type = 1
  UnderTolerance = 0
  X = 8.40752
  Y = -49.8735
FEATURE [TechDraw::DrawViewDimension] Dimension008
  AngleOverride = false
  Arbitrary = false
  ArbitraryTolerances = false
  BoxCorners = (2) [(-6,-37.2394,-1e-07),(6,37.2394,1e-07)]
  EqualTolerance = true
  ExtensionAngle = 0
  FormatSpec = %.2w
  FormatSpecOverTolerance = %+.2w
  FormatSpecUnderTolerance = %+.2w
  Inverted = false
  LineAngle = 0
  LockPosition = false
  MeasureType = 1
  OverTolerance = 0
  References2D = -> [ProjItem]
  Rotation = 0
  ScaleType = 0
  TheoreticalExact = false
  Type = 2
  UnderTolerance = 0
  X = 21.0174
  Y = -28.9242
FEATURE [TechDraw::DrawViewDimension] Dimension009
  AngleOverride = false
  Arbitrary = false
  ArbitraryTolerances = false
  BoxCorners = (2) [(-7.5,-46.5492,-1e-07),(7.5,46.5492,1e-07)]
  EqualTolerance = true
  ExtensionAngle = 0
  FormatSpec = %.2w
  FormatSpecOverTolerance = %+.2w
  FormatSpecUnderTolerance = %+.2w
  Inverted = false
  LineAngle = 0
  LockPosition = false
  MeasureType = 1
  OverTolerance = 0
  References2D = -> [ProjItem]
  Rotation = 0
  ScaleType = 0
  TheoreticalExact = false
  Type = 0
  UnderTolerance = 0
  X = 25.7787
  Y = 8.98125
FEATURE [TechDraw::DrawViewDimension] Dimension010
  AngleOverride = false
  Arbitrary = false
  ArbitraryTolerances = false
  BoxCorners = (2) [(-7.5,-46.5492,-1e-07),(7.5,46.5492,1e-07)]
  EqualTolerance = true
  ExtensionAngle = 0
  FormatSpec = ⌀%.2w
  FormatSpecOverTolerance = %+.2w
  FormatSpecUnderTolerance = %+.2w
  Inverted = false
  LineAngle = 0
  LockPosition = false
  MeasureType = 1
  OverTolerance = 0
  References2D = -> [ProjItem]
  Rotation = 0
  ScaleType = 0
  TheoreticalExact = false
  Type = 5
  UnderTolerance = 0
  X = -20.7774
  Y = 8.40133
FEATURE [TechDraw::DrawViewDimension] Dimension011
  AngleOverride = false
  Arbitrary = false
  ArbitraryTolerances = false
  BoxCorners = (2) [(-7.5,-46.5492,-1e-07),(7.5,46.5492,1e-07)]
  EqualTolerance = true
  ExtensionAngle = 0
  FormatSpec = R%.2w
  FormatSpecOverTolerance = %+.2w
  FormatSpecUnderTolerance = %+.2w
  Inverted = false
  LineAngle = 0
  LockPosition = false
  MeasureType = 1
  OverTolerance = 0
  References2D = -> [ProjItem]
  Rotation = 0
  ScaleType = 0
  TheoreticalExact = false
  Type = 4
  UnderTolerance = 0
  X = -21.5494
  Y = -6.41734
FEATURE [TechDraw::DrawViewDimension] Dimension012
  AngleOverride = false
  Arbitrary = false
  ArbitraryTolerances = false
  BoxCorners = (2) [(-46.5492,-14.625,-1e-07),(46.5492,14.625,1e-07)]
  EqualTolerance = true
  ExtensionAngle = 0
  FormatSpec = %.2w
  FormatSpecOverTolerance = %+.2w
  FormatSpecUnderTolerance = %+.2w
  Inverted = false
  LineAngle = 0
  LockPosition = false
  MeasureType = 1
  OverTolerance = 0
  References2D = -> [ProjItem001]
  Rotation = 0
  ScaleType = 0
  TheoreticalExact = false
  Type = 0
  UnderTolerance = 0
  X = 38.2148
  Y = 16.1916
FEATURE [TechDraw::DrawViewDimension] Dimension013
  AngleOverride = false
  Arbitrary = false
  ArbitraryTolerances = false
  BoxCorners = (2) [(-46.5492,-14.625,-1e-07),(46.5492,14.625,1e-07)]
  EqualTolerance = true
  ExtensionAngle = 0
  FormatSpec = %.2w
  FormatSpecOverTolerance = %+.2w
  FormatSpecUnderTolerance = %+.2w
  Inverted = false
  LineAngle = 0
  LockPosition = false
  MeasureType = 1
  OverTolerance = 0
  References2D = -> [ProjItem001]
  Rotation = 0
  ScaleType = 0
  TheoreticalExact = false
  Type = 0
  UnderTolerance = 0
  X = 10.4194
  Y = -29.8383
FEATURE [TechDraw::DrawViewDimension] Dimension014
  AngleOverride = false
  Arbitrary = false
  ArbitraryTolerances = false
  BoxCorners = (2) [(-46.5492,-14.625,-1e-07),(46.5492,14.625,1e-07)]
  EqualTolerance = true
  ExtensionAngle = 0
  FormatSpec = R%.2w
  FormatSpecOverTolerance = %+.2w
  FormatSpecUnderTolerance = %+.2w
  Inverted = false
  LineAngle = 0
  LockPosition = false
  MeasureType = 1
  OverTolerance = 0
  References2D = -> [ProjItem001]
  Rotation = 0
  ScaleType = 0
  TheoreticalExact = false
  Type = 4
  UnderTolerance = 0
  X = -30.1306
  Y = -10.0439
FEATURE [TechDraw::DrawPage] Page
  KeepUpdated = true
  NextBalloonIndex = 1
  ProjectionType = 0
  Template = -> Template
  Views = -> [ProjGroup,Dimension,Dimension001,Dimension002,Dimension003,Dimension004,Dimension005,Dimension006,Dimension007,Dimension008,Dimension009,Dimension010,Dimension011,Dimension012,Dimension013,Dimension014]
